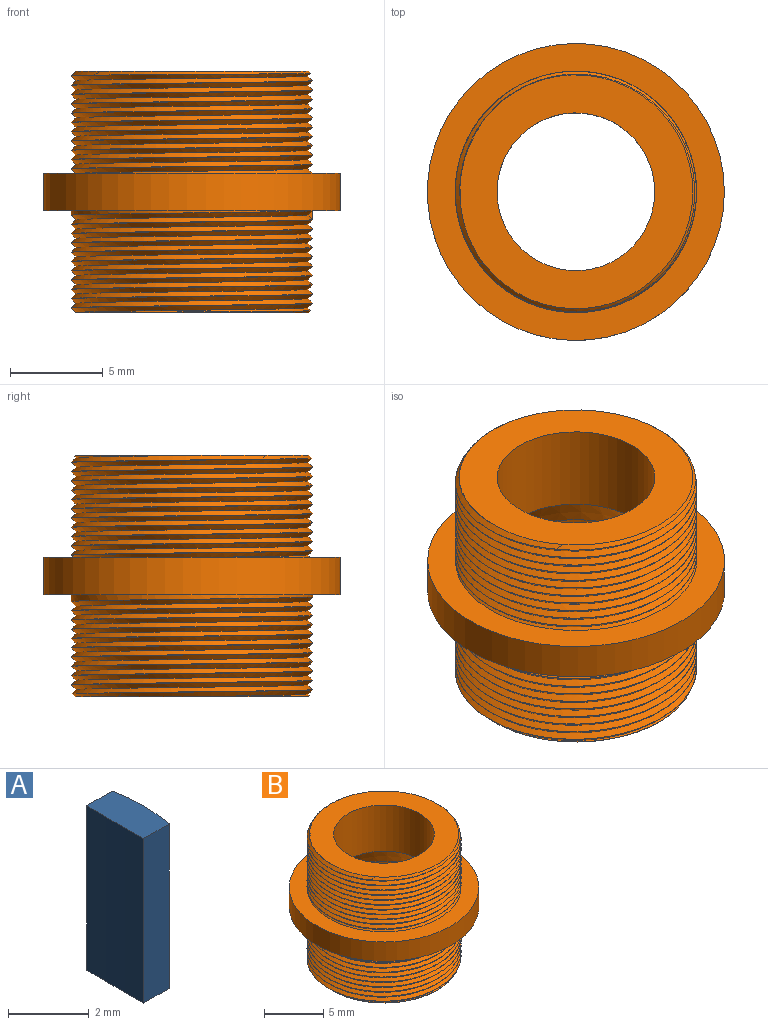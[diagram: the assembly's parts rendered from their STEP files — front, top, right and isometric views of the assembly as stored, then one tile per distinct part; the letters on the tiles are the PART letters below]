
ASSEMBLY  parts=2 mates=1
PART A: 6 faces, bbox 1x2x5 mm
  f0: plane 5x0.89mm, normal (0,-1,0), area 4.5mm2, adj f1,f3,f4,f5
  f1: cylinder r=5.25mm len=5mm, axis (0,0,-1), area 10.1mm2, adj f0,f2,f4,f5
  f2: plane 5x0.89mm, normal (0,1,0), area 4.5mm2, adj f1,f3,f4,f5
  f3: cylinder r=53mm len=5mm, axis (0,0,-1), area 10mm2, adj f0,f2,f4,f5
  f4: plane 2x1mm, normal (0,0,1), area 1.9mm2, adj f0,f1,f2,f3
  f5: plane 2x1mm, normal (0,0,-1), area 1.9mm2, adj f0,f1,f2,f3
PART B: 19 faces, bbox 16.1x16.1x13.7 mm
  f0: cylinder r=6.5mm len=13mm, axis (0,0,1), area 27.3mm2, adj f1,f15,f16,f17,f18
  f1: plane 16x16mm, normal (0,0,-1), area 68.3mm2, adj f0,f2
  f2: cylinder r=8mm len=16mm, axis (0,0,1), area 100.5mm2, adj f1,f3
  f3: plane 16x16mm, normal (0,0,1), area 68.3mm2, adj f2,f4,f14
  f4: cylinder r=6.5mm len=13mm, axis (0,0,1), area 4.4mm2, adj f3,f10,f11,f12
  f5: plane 12.69x12.65mm, normal (0,0,1), area 67.7mm2, adj f6,f10,f11,f12
  f6: cylinder r=4.25mm len=8.5mm, axis (0,0,1), area 127.3mm2, adj f5,f7
  f7: cone r=5.25mm half-angle=30deg, axis (0,0,-1), area 59.7mm2, adj f6,f8
  f8: cylinder r=5.25mm len=10.5mm, axis (0,0,1), area 214.4mm2, adj f7,f9
  f9: plane 12.69x12.65mm, normal (0,0,-1), area 37.9mm2, adj f8,f15,f16,f17
  f10: cone r=6.3mm half-angle=45deg, axis (0,0,-1), area 4.7mm2, adj f4,f5,f11,f12
  f11: bspline ~15.01x13mm, area 162.6mm2, adj f4,f5,f10,f12,f13,f14
  f12: bspline ~15.01x13mm, area 155.3mm2, adj f4,f5,f10,f11,f13,f14
  f13: plane 0.49x0.25mm, normal (0,1,0), area 0.1mm2, adj f11,f12,f14
  f14: cylinder r=6.5mm len=13mm, axis (0,0,-1), area 10.2mm2, adj f3,f11,f12,f13
  f15: cone r=6.5mm half-angle=45deg, axis (0,0,1), area 4.7mm2, adj f0,f9,f16,f17
  f16: bspline ~15.01x13mm, area 148.5mm2, adj f0,f9,f15,f17,f18
  f17: bspline ~15.01x13mm, area 141.9mm2, adj f0,f9,f15,f16,f18
  f18: plane 0.49x0.25mm, normal (0,-1,0), area 0.1mm2, adj f0,f16,f17
PLACE A t=(-1.13,-0.37,-5.49)mm
PLACE B t=(-5.28,-0.37,1.01)mm fixed
MATE slider A.f1 <-> B.f0  axis (0,0,-1) through (-5.28,-0.37,-5.49)mm
